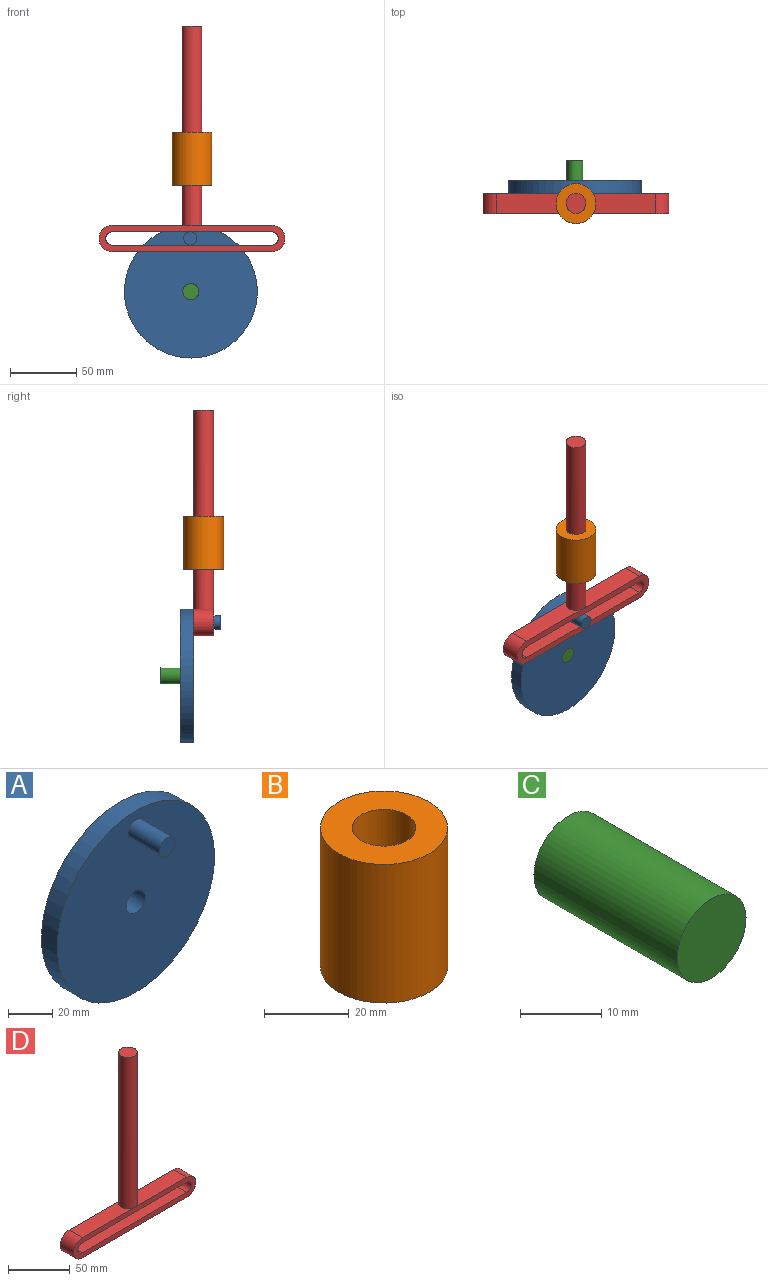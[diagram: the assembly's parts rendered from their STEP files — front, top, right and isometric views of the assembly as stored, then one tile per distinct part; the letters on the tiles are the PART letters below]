
ASSEMBLY  parts=4 mates=2
PART A: 6 faces, bbox 100x30x100 mm
  f0: cylinder r=6mm len=12mm, axis (0,-1,0), area 377mm2, adj f2,f3
  f1: cylinder r=50mm len=100mm, axis (0,-1,0), area 3141.6mm2, adj f2,f3
  f2: plane 100x100mm, normal (0,1,0), area 7740.9mm2, adj f0,f1
  f3: plane 100x100mm, normal (0,-1,0), area 7662.3mm2, adj f0,f1,f4
  f4: cylinder r=5mm len=20mm, axis (0,1,0), area 628.3mm2, adj f3,f5
  f5: plane 10x10mm, normal (0,-1,0), area 78.5mm2, adj f4
PART B: 4 faces, bbox 30x30x40 mm
  f0: cylinder r=7.5mm len=40mm, axis (0,0,1), area 1885mm2, adj f2,f3
  f1: cylinder r=15mm len=40mm, axis (0,0,1), area 3769.9mm2, adj f2,f3
  f2: plane 30x30mm, normal (0,0,-1), area 530.1mm2, adj f0,f1
  f3: plane 30x30mm, normal (0,0,1), area 530.1mm2, adj f0,f1
PART C: 3 faces, bbox 12x25x12 mm
  f0: cylinder r=6mm len=25mm, axis (0,-1,0), area 942.5mm2, adj f1,f2
  f1: plane 12x12mm, normal (0,1,0), area 113.1mm2, adj f0
  f2: plane 12x12mm, normal (0,-1,0), area 113.1mm2, adj f0
PART D: 13 faces, bbox 140x15x170 mm
  f0: plane 60x15mm, normal (0,0,1), area 811.6mm2, adj f1,f9,f10,f11
  f1: cylinder r=10mm len=20mm, axis (0,1,0), area 471.2mm2, adj f0,f8,f9,f10
  f2: plane 60x15mm, normal (0,0,1), area 811.6mm2, adj f3,f9,f10,f11
  f3: cylinder r=10mm len=20mm, axis (0,1,0), area 471.2mm2, adj f2,f8,f9,f10
  f4: plane 120x15mm, normal (0,0,-1), area 1800mm2, adj f5,f7,f9,f10
  f5: cylinder r=5mm len=15mm, axis (0,1,0), area 235.6mm2, adj f4,f6,f9,f10
  f6: plane 120x15mm, normal (0,0,1), area 1800mm2, adj f5,f7,f9,f10
  f7: cylinder r=5mm len=15mm, axis (0,1,0), area 235.6mm2, adj f4,f6,f9,f10
  f8: plane 120x15mm, normal (0,0,-1), area 1800mm2, adj f1,f3,f9,f10
  f9: plane 140x20mm, normal (0,-1,0), area 1435.6mm2, adj f0,f1,f2,f3,f4,f5,f6,f7
  f10: plane 140x20mm, normal (0,1,0), area 1435.6mm2, adj f0,f1,f2,f3,f4,f5,f6,f7
  f11: cylinder r=7.5mm len=150mm, axis (0,0,-1), area 7068.6mm2, adj f0,f2,f12
  f12: plane 15x15mm, normal (0,0,1), area 176.7mm2, adj f11
PLACE A rot(axis=(0,-1,0),0.6deg) t=(0,0,-0.08)mm
PLACE B t=(0.85,-0.15,0)mm fixed
PLACE C at identity fixed
PLACE D t=(0.85,-0.15,0)mm
MATE revolute A.f0 <-> C.f0  axis (0,-1,0) through (7.5,7.5,0)mm
MATE slider D.f11 <-> B.f0  axis (0,0,-1) through (8.35,-0.15,80)mm
